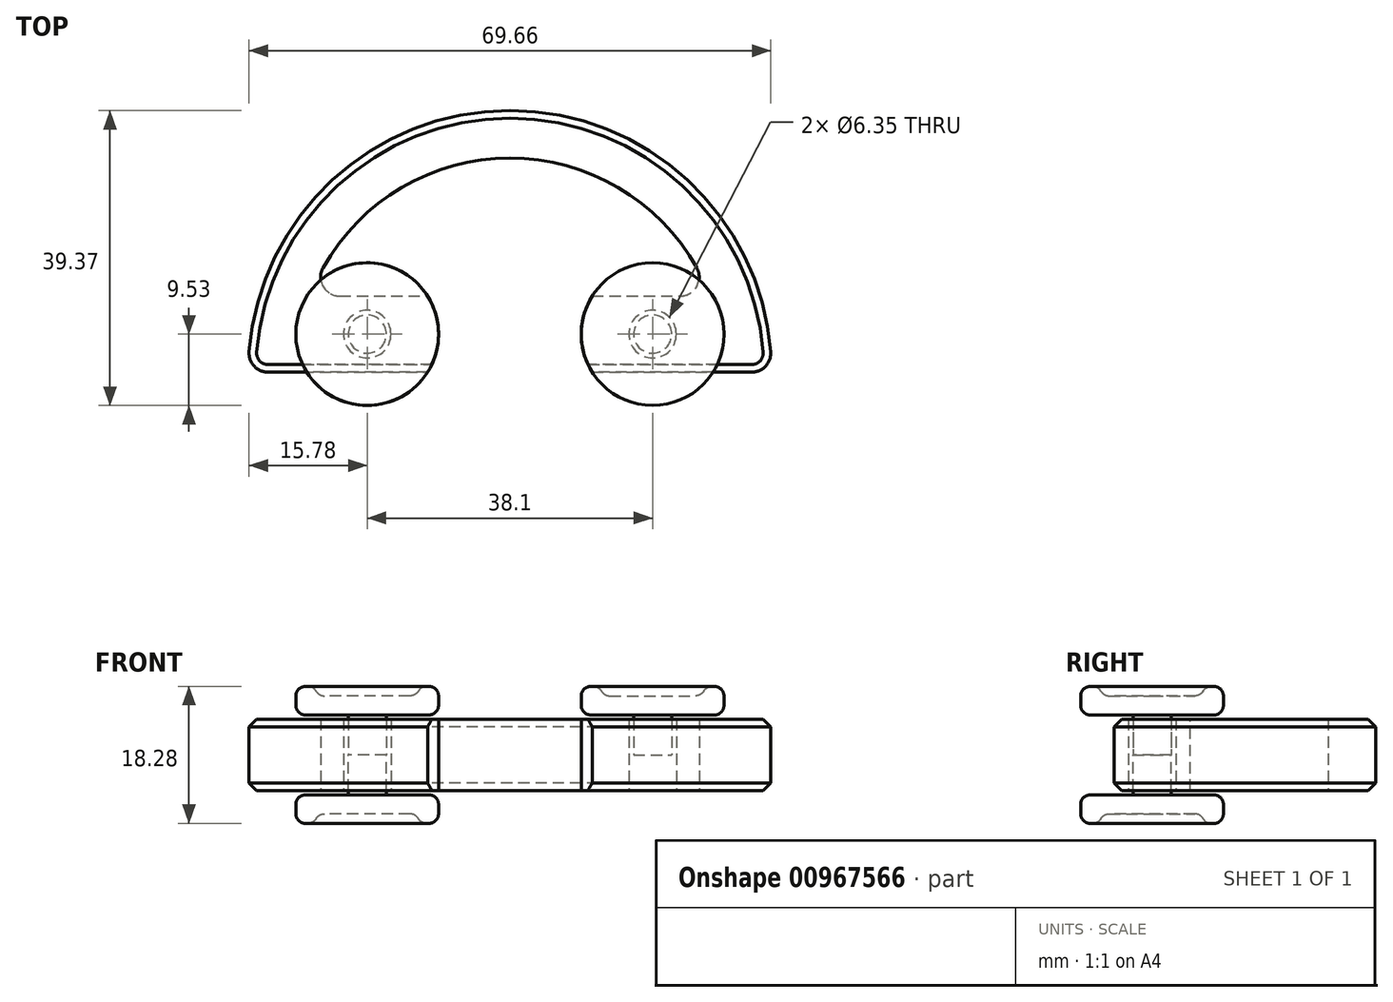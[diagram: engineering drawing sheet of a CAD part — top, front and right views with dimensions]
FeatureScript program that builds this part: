
annotation { "Feature Type Name" : "Feature", "Feature Type Description" : "" }
export const myFeature = defineFeature(function(context is Context, id is Id, definition is map)
    precondition{}
    {
        {
            var Q0;
            Q0=qCreatedBy(makeId("Top.planeOp"),FACE);
            var sketch = newSketch(context, id + "F0", { "sketchPlane" : qUnion([Q0])});
            skCircle(sketch, "E0", {"center": v(-19.05, 0) * mm, "radius": 9.53 * mm});
            skCircle(sketch, "E1", {"center": v(19.05, 0) * mm, "radius": 9.53 * mm});
            skCircle(sketch, "E2", {"center": v(-19.05, 0) * mm, "radius": 3.18 * mm});
            skCircle(sketch, "E3", {"center": v(19.05, 0) * mm, "radius": 3.18 * mm});
            skLineSegment(sketch, "E4", {"start": v(-34.93, -5.08) * mm, "end": v(34.93, -5.08) * mm});
            skArc(sketch, "E5", {"start": v(34.93, -5.08) * mm, "mid": v(0, 29.85) * mm, "end": v(-34.93, -5.08) * mm});
            skLineSegment(sketch, "E6", {"start": v(-26.7, 5.08) * mm, "end": v(26.7, 5.08) * mm});
            skArc(sketch, "E7", {"start": v(26.7, 5.08) * mm, "mid": v(0, 23.5) * mm, "end": v(-26.7, 5.08) * mm});
            skSolve(sketch);
        }
        {
            var Q0;
            {var subQ0=sQuery(id+"F0.wireOp",EDGE,"E5");Q0=makeQuery(id+"F0.imprint","IMPRINT",FACE,{"disambiguationData":[TD([[makeQuery(id+"F0.imprint","IMPRINT",EDGE,{"derivedFrom":subQ0}),1.0]])]});}
            var Q1;
            Q1=makeQuery(id+"F0.imprint","IMPRINT",FACE,{"disambiguationData":[TD([[makeQuery(id+"F0.imprint","IMPRINT",EDGE,{"derivedFrom":sQuery(id+"F0.wireOp",EDGE,"E2")}),-1.0]])]});
            var Q2;
            {var subQ0=sQuery(id+"F0.wireOp",EDGE,"E4");var subQ1=sQuery(id+"F0.wireOp",EDGE,"E0");var subQ2=makeQuery(id+"F0.imprint","INTERSECT",VERTEX,{"disambiguationData":[OD(1.0)],"derivedFrom":[subQ1,subQ0]});Q2=makeQuery(id+"F0.imprint","IMPRINT",FACE,{"disambiguationData":[TD([[makeQuery(id+"F0.imprint","IMPRINT",EDGE,{"disambiguationData":[TD([[subQ2,-1.0]])],"derivedFrom":subQ1}),-1.0]])]});}
            var Q3;
            Q3=makeQuery(id+"F0.imprint","IMPRINT",FACE,{"disambiguationData":[TD([[makeQuery(id+"F0.imprint","IMPRINT",EDGE,{"derivedFrom":sQuery(id+"F0.wireOp",EDGE,"E3")}),-1.0]])]});
            extrude(context, id + "F1", {"entities" : qUnion([Q0, Q1, Q2, Q3]), "endBound" : BoundingType.SYMMETRIC, "depth" : 9.52 * mm, "offsetDistance" : 25.4 * mm});
        }
        {
            var Q0;
            {var subQ0=sQuery(id+"F0.wireOp",EDGE,"E7");var subQ1=sQuery(id+"F0.wireOp",EDGE,"E6");Q0=makeQuery(id+"F1.opExtrude","SWEPT_EDGE",EDGE,{"disambiguationData":[OSD([subQ1,subQ0]),TDD([makeQuery(id+"F0.imprint","INTERSECT",VERTEX,{"disambiguationData":[OD(1.0)],"derivedFrom":[subQ1,subQ0]})])]});}
            var Q1;
            {var subQ0=sQuery(id+"F0.wireOp",EDGE,"E7");var subQ1=sQuery(id+"F0.wireOp",EDGE,"E6");Q1=makeQuery(id+"F1.opExtrude","SWEPT_EDGE",EDGE,{"disambiguationData":[OSD([subQ1,subQ0]),TDD([makeQuery(id+"F0.imprint","INTERSECT",VERTEX,{"disambiguationData":[OD(0.0)],"derivedFrom":[subQ1,subQ0]})])]});}
            fillet(context, id + "F2", {"entities" : qUnion([Q0, Q1]), "radius" : 2.54 * mm, "tangentPropagation" : true, "allowEdgeOverflow" : false});
        }
        {
            var Q0;
            Q0=qCreatedBy(makeId("Top.planeOp"),FACE);
            cPlane(context, id + "F3", {"entities" : qUnion([Q0]), "cplaneType" : CPlaneType.OFFSET, "offset" : 5.33 * mm, "width" : 152.4 * mm, "height" : 152.4 * mm});
        }
        {
            var Q0;
            Q0=qCreatedBy(id+"F3.planeOp",FACE);
            var sketch = newSketch(context, id + "F4", { "sketchPlane" : qUnion([Q0])});
            skCircle(sketch, "E8", {"center": v(-19.05, 0) * mm, "radius": 9.53 * mm});
            skCircle(sketch, "E9", {"center": v(19.05, 0) * mm, "radius": 9.53 * mm});
            skSolve(sketch);
        }
        {
            var Q0;
            Q0=makeQuery(id+"F4.imprint","IMPRINT",FACE,{"disambiguationData":[TD([[makeQuery(id+"F4.imprint","IMPRINT",EDGE,{"derivedFrom":sQuery(id+"F4.wireOp",EDGE,"E8")}),1.0]])]});
            extrude(context, id + "F5", {"entities" : qUnion([Q0]), "depth" : 3.8 * mm, "offsetDistance" : 25.4 * mm});
        }
        {
            var Q0;
            Q0=qCreatedBy(makeId("Top.planeOp"),FACE);
            var sketch = newSketch(context, id + "F6", { "sketchPlane" : qUnion([Q0])});
            skCircle(sketch, "E10", {"center": v(-19.05, 0) * mm, "radius": 2.54 * mm});
            skSolve(sketch);
        }
        {
            var Q0;
            Q0 = qSketchRegion(id + "F6", true);
            var Q1;
            Q1=makeQuery(id+"F5.opExtrude","CAP_FACE",FACE,{"disambiguationData":[OSD([sQuery(id+"F4.wireOp",EDGE,"E8")])],"isStart":false});
            extrude(context, id + "F7", {"entities" : qUnion([Q0]), "operationType" : NewBodyOperationType.ADD, "endBound" : BoundingType.UP_TO_SURFACE, "depth" : 25.4 * mm, "endBoundEntityFace" : qUnion([Q1]), "offsetDistance" : 25.4 * mm});
        }
        {
            var Q0;
            Q0=makeQuery(id+"F5.opExtrude","CAP_FACE",FACE,{"disambiguationData":[OSD([sQuery(id+"F4.wireOp",EDGE,"E8")])],"isStart":false});
            var sketch = newSketch(context, id + "F8", { "sketchPlane" : qUnion([Q0])});
            skCircle(sketch, "E11", {"center": v(-19.05, 0) * mm, "radius": 6.65 * mm});
            skSolve(sketch);
        }
        {
            var Q0;
            Q0 = qSketchRegion(id + "F8", true);
            extrude(context, id + "F9", {"entities" : qUnion([Q0]), "operationType" : NewBodyOperationType.REMOVE, "oppositeDirection" : true, "depth" : 1.27 * mm, "offsetDistance" : 25.4 * mm});
        }
        {
            var Q0;
            Q0=makeQuery(id+"F5.opExtrude","CAP_FACE",FACE,{"disambiguationData":[OSD([sQuery(id+"F4.wireOp",EDGE,"E8")])],"isStart":false});
            var Q1;
            Q1=makeQuery(id+"F5.opExtrude","CAP_EDGE",EDGE,{"disambiguationData":[OSD([sQuery(id+"F4.wireOp",EDGE,"E8")])],"isStart":true});
            fillet(context, id + "F10", {"entities" : qUnion([Q0, Q1]), "radius" : 1.27 * mm, "tangentPropagation" : true, "allowEdgeOverflow" : false});
        }
        {
            var Q0;
            Q0=makeQuery(id+"F9.boolean.opBoolean","COPY",FACE,{"derivedFrom":makeQuery(id+"F9.opExtrude","CAP_FACE",FACE,{"disambiguationData":[OSD([sQuery(id+"F8.wireOp",EDGE,"E11")])],"isStart":false})});
            var Q1;
            {var subQ0=sQuery(id+"F8.wireOp",EDGE,"E11");Q1=makeQuery(id+"F10.opFillet","BLEND_EDGE",EDGE,{"blendedFrom":[makeQuery(id+"F9.boolean.opBoolean","COPY",EDGE,{"derivedFrom":makeQuery(id+"F9.opExtrude","CAP_EDGE",EDGE,{"disambiguationData":[OSD([subQ0])],"isStart":true})}),makeQuery(id+"F9.boolean.opBoolean","COPY",FACE,{"derivedFrom":makeQuery(id+"F9.opExtrude","CAP_FACE",FACE,{"disambiguationData":[OSD([subQ0])],"isStart":false})})],"blendedInto":[makeQuery(id+"F9.boolean.opBoolean","COPY",FACE,{"derivedFrom":makeQuery(id+"F9.opExtrude","CAP_FACE",FACE,{"disambiguationData":[OSD([subQ0])],"isStart":false})})]});}
            fillet(context, id + "F11", {"entities" : qUnion([Q0, Q1]), "radius" : 1.27 * mm, "tangentPropagation" : true, "allowEdgeOverflow" : false});
        }
        {
            var Q0;
            Q0=makeQuery(id+"F5.opExtrude","SWEPT_BODY",BODY,{"disambiguationData":[OSD([sQuery(id+"F4.wireOp",EDGE,"E8")])]});
            var Q1;
            Q1=qCreatedBy(makeId("Top.planeOp"),FACE);
            mirror(context, id + "F12", {"operationType" : NewBodyOperationType.ADD, "entities" : qUnion([Q0]), "mirrorPlane" : qUnion([Q1])});
        }
        {
            var Q0;
            Q0=makeQuery(id+"F5.opExtrude","SWEPT_BODY",BODY,{"disambiguationData":[OSD([sQuery(id+"F4.wireOp",EDGE,"E8")])]});
            var Q1;
            Q1=qCreatedBy(makeId("Right.planeOp"),FACE);
            mirror(context, id + "F13", {"entities" : qUnion([Q0]), "mirrorPlane" : qUnion([Q1])});
        }
        {
            var Q0;
            {var subQ0=sQuery(id+"F0.wireOp",EDGE,"E5");var subQ1=sQuery(id+"F0.wireOp",EDGE,"E4");Q0=makeQuery(id+"F1.opExtrude","SWEPT_EDGE",EDGE,{"disambiguationData":[OSD([subQ1,subQ0]),TDD([makeQuery(id+"F0.imprint","INTERSECT",VERTEX,{"disambiguationData":[OD(0.0)],"derivedFrom":[subQ1,subQ0]})])]});}
            var Q1;
            {var subQ0=sQuery(id+"F0.wireOp",EDGE,"E5");var subQ1=sQuery(id+"F0.wireOp",EDGE,"E4");Q1=makeQuery(id+"F1.opExtrude","SWEPT_EDGE",EDGE,{"disambiguationData":[OSD([subQ1,subQ0]),TDD([makeQuery(id+"F0.imprint","INTERSECT",VERTEX,{"disambiguationData":[OD(1.0)],"derivedFrom":[subQ1,subQ0]})])]});}
            fillet(context, id + "F14", {"entities" : qUnion([Q0, Q1]), "radius" : 2.54 * mm, "tangentPropagation" : true, "allowEdgeOverflow" : false});
        }
        {
            var Q0;
            Q0=makeQuery(id+"F1.opExtrude","CAP_EDGE",EDGE,{"disambiguationData":[OSD([sQuery(id+"F0.wireOp",EDGE,"E5")])],"isStart":false});
            var Q1;
            Q1=makeQuery(id+"F1.opExtrude","CAP_EDGE",EDGE,{"disambiguationData":[OSD([sQuery(id+"F0.wireOp",EDGE,"E5")])],"isStart":true});
            chamfer(context, id + "F15", {"entities" : qUnion([Q0, Q1]), "width" : 1.02 * mm, "tangentPropagation" : true});
        }
    });
